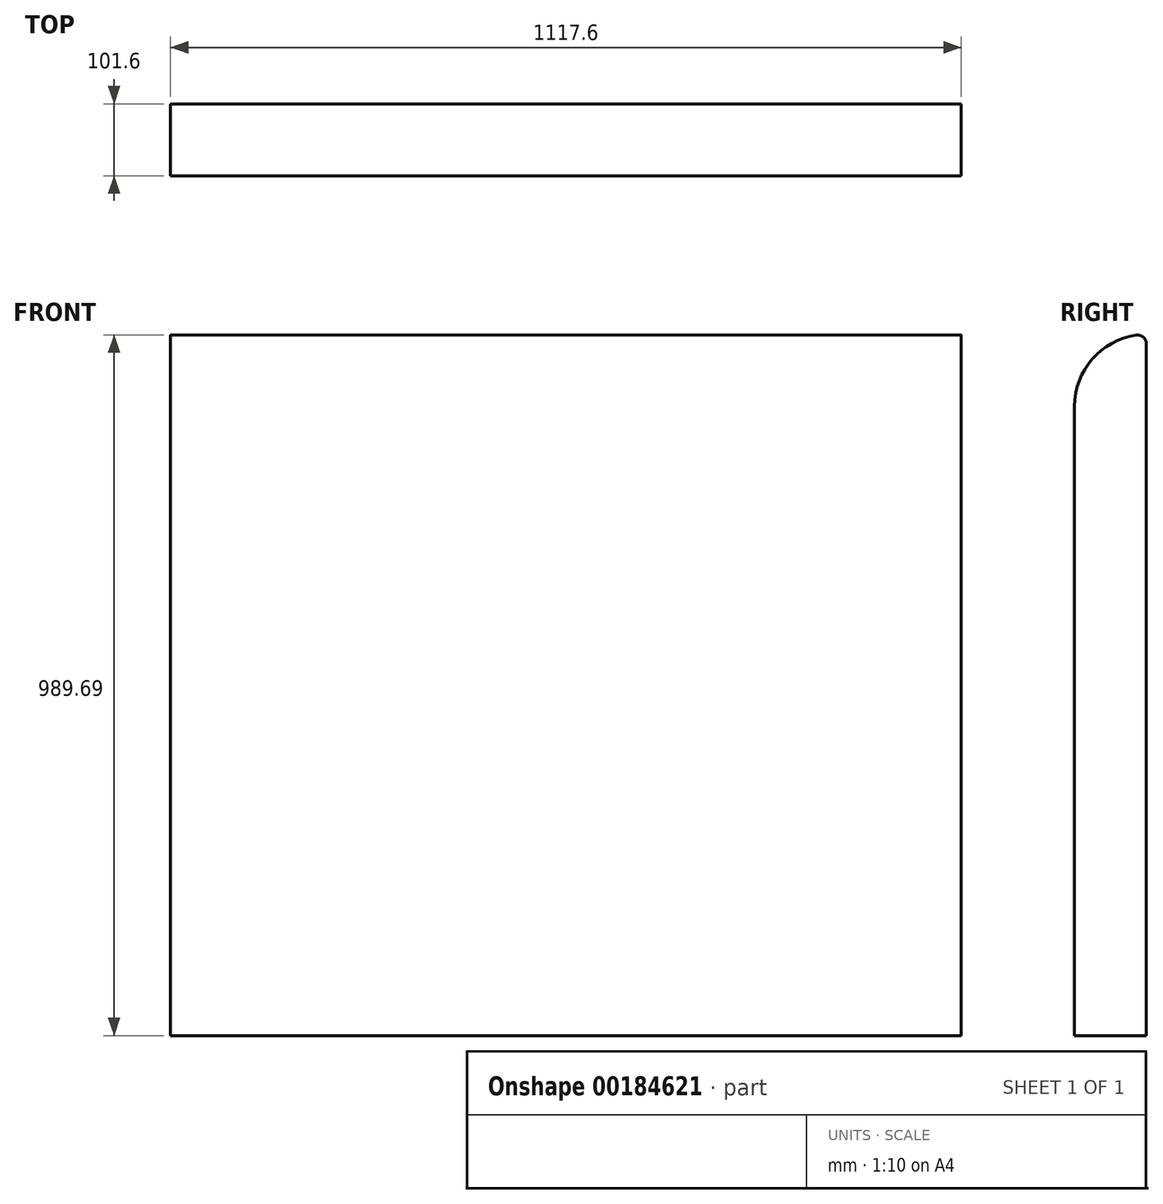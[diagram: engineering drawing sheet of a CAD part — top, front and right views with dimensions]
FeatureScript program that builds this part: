
annotation { "Feature Type Name" : "Feature", "Feature Type Description" : "" }
export const myFeature = defineFeature(function(context is Context, id is Id, definition is map)
    precondition{}
    {
        {
            var Q0;
            Q0=qCreatedBy(makeId("Right.planeOp"),FACE);
            var sketch = newSketch(context, id + "F0", { "sketchPlane" : qUnion([Q0])});
            skLineSegment(sketch, "E0.bottom", {"start": v(50.8, -495.3) * mm, "end": v(-50.8, -495.3) * mm});
            skLineSegment(sketch, "E0.top", {"start": v(50.8, 495.3) * mm, "end": v(-50.8, 495.3) * mm});
            skLineSegment(sketch, "E0.left", {"start": v(50.8, -495.3) * mm, "end": v(50.8, 495.3) * mm});
            skLineSegment(sketch, "E0.right", {"start": v(-50.8, -495.3) * mm, "end": v(-50.8, 495.3) * mm});
            skPoint(sketch, "E0.middle", {"position": v(0, 0) * mm});
            skPoint(sketch, "E1", {"position": v(-50.8, -206.42) * mm});
            skSolve(sketch);
        }
        {
            var Q0;
            Q0 = qSketchRegion(id + "F0", true);
            extrude(context, id + "F1", {"entities" : qUnion([Q0]), "endBound" : BoundingType.SYMMETRIC, "depth" : 1117.6 * mm});
        }
        {
            var Q0;
            Q0=makeQuery(id+"F1.opExtrude","SWEPT_EDGE",EDGE,{"disambiguationData":[OSD([sQuery(id+"F0.wireOp",EDGE,"E0.top"),sQuery(id+"F0.wireOp",EDGE,"E0.right")])]});
            fillet(context, id + "F2", {"entities" : qUnion([Q0]), "radius" : 101.6 * mm, "tangentPropagation" : true, "allowEdgeOverflow" : false});
        }
        {
            var Q0;
            Q0=makeQuery(id+"F2.opFillet","BLEND_EDGE",EDGE,{"blendedFrom":[makeQuery(id+"F1.opExtrude","SWEPT_EDGE",EDGE,{"disambiguationData":[OSD([sQuery(id+"F0.wireOp",EDGE,"E0.top"),sQuery(id+"F0.wireOp",EDGE,"E0.right")])]}),makeQuery(id+"F1.opExtrude","SWEPT_FACE",FACE,{"disambiguationData":[OSD([sQuery(id+"F0.wireOp",EDGE,"E0.left")])]})],"blendedInto":[makeQuery(id+"F1.opExtrude","SWEPT_FACE",FACE,{"disambiguationData":[OSD([sQuery(id+"F0.wireOp",EDGE,"E0.left")])]})]});
            fillet(context, id + "F3", {"entities" : qUnion([Q0]), "radius" : 12.7 * mm, "tangentPropagation" : true, "allowEdgeOverflow" : false});
        }
    });
